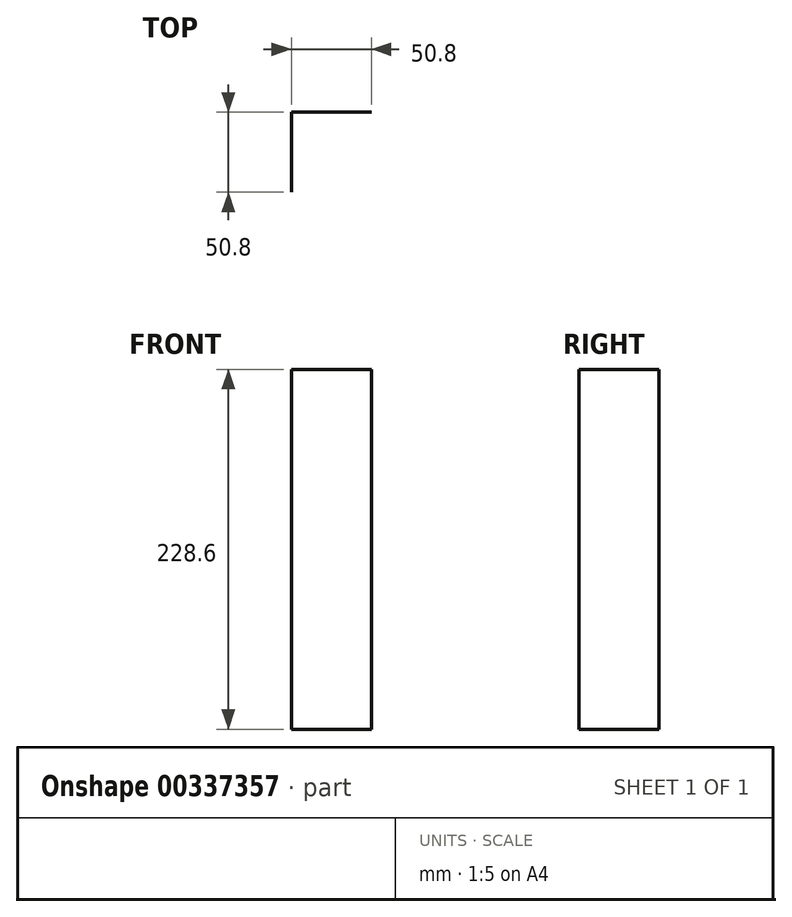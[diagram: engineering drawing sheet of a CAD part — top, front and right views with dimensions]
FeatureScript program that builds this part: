
annotation { "Feature Type Name" : "Feature", "Feature Type Description" : "" }
export const myFeature = defineFeature(function(context is Context, id is Id, definition is map)
    precondition{}
    {
        {
            var Q0;
            Q0=qCreatedBy(makeId("Top.planeOp"),FACE);
            var sketch = newSketch(context, id + "F0", { "sketchPlane" : qUnion([Q0])});
            skLineSegment(sketch, "E0", {"start": v(-91.08, -101.6) * mm, "end": v(-91.08, -50.8) * mm});
            skLineSegment(sketch, "E1", {"start": v(-91.08, -50.8) * mm, "end": v(-40.28, -50.8) * mm});
            skSolve(sketch);
        }
        {
            var Q0;
            Q0 = qSketchRegion(id + "F0", true);
            var Q1;
            Q1=sQuery(id+"F0.wireOp",EDGE,"E0");
            var Q2;
            Q2=sQuery(id+"F0.wireOp",EDGE,"E1");
            extrude(context, id + "F1", {"entities" : qUnion([Q0]), "bodyType" : ToolBodyType.SURFACE, "surfaceEntities" : qUnion([Q1, Q2]), "depth" : 228.6 * mm});
        }
    });
